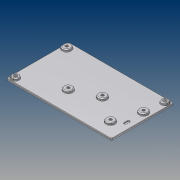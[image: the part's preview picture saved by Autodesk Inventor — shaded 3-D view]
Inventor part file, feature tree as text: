
AUTODESK INVENTOR PART (.ipt)
format: ipt  version: 2012 (Build 160160000, 160)  size: 629,248 bytes
history: native  units: mm (DEFAULTED — no unit token found)
features: sketch x7, extrude x6, fillet x4, plane x3, hole x1, other x1, shell x1, projected_geometry x1
ambient origin geometry x5: Origin, X Axis, Y Axis, Z Axis, Center Point
bodies: Solid1 (feature_tree)
feature tree (24):
  extrude  "Base Profile"  Depth=125.1204mm
  extrude  "Extra Material for Screw Holes"  Depth=2.032mm
  hole  "Screw Holes"  [1 undecoded]
  extrude  "Extrusion3"  Depth=0.523599mm
  other  "Screw Hole Drafts"
  shell  "Screw Hole Shell"  Thickness=4.699mm
  extrude  "Velcro Cut"  Depth=31.75mm
  extrude  "Side Edge Clearance Cut"  Depth=57.15mm
  extrude  "Extrusion6"  Depth=54.61mm
  fillet  "Bottom Fillet 1"  Radius=8.89mm
  fillet  "Bottom Fillet 2"  Radius=20.32mm
  fillet  "Top Fillet 1"  Radius=44.45mm
  fillet  "Top Fillet 2"  [1 undecoded]
  plane  "YZ Plane (RIGHT)"
  plane  "XZ Plane (TOP)"
  plane  "XY Plane (FRONT)"
  sketch  "Sketch2"  dims[d0=74.3204mm d1=125.1204mm]
  sketch  "Sketch3"  dims[d2=1.778mm d3=2.032mm d4=-0.523599mm]
  sketch  "Sketch4"  dims[d5=2.4892mm d6=0.0mm]
  sketch  "Sketch5"  dims[d7=3.9624mm d8=12.7mm d9=6.477mm d10=2.4892mm d11=14.3117mm d12=19.05mm d13=20.594885mm d14=2.032mm]
  sketch  "Sketch6"  dims[d15=25.4mm d16=-0.349066mm d17=0.523599mm d18=4.699mm]
  sketch  "Sketch7"  dims[d19=57.15mm d20=31.75mm]
  projected_geometry  "Projected Loop1"
  sketch  "Sketch8"  dims[d21=31.75mm d22=57.15mm d23=54.61mm d24=8.89mm d25=20.32mm d26=44.45mm d27=0.0mm d28=14.605mm d29=12.7mm d30=13.335mm d31=29.21mm d32=57.15mm d33=20.0mm d35=360.0deg d39=34.925mm d40=6.35mm d41=0.762mm d42=-7.853982mm d43=0.762mm d44=27.94mm d45=44.45mm d46=1.27mm d47=0.762mm d48=0.523599mm d49=0.762mm d50=-1.745329mm d51=53.4416mm d52=2.54mm d53=6.0198mm d54=7.9502mm d55=3.175mm d56=0.79375mm d57=0.79375mm d58=0.254mm d59=0.79375mm d60=1.5875mm d61=0.396875mm d62=1.5875mm d63=0.79375mm d64=0.396875mm d65=0.396875mm d66=0.79375mm]
note: 2 required parameter values undecoded (feature->parameter linkage not recoverable at this tier; creation-order binding heuristic only, values carry confidence <= 0.55)
